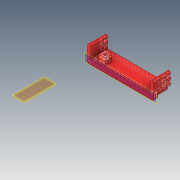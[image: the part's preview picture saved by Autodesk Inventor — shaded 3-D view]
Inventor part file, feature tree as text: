
AUTODESK INVENTOR PART (.ipt)
format: ipt  version: 2019 (Build 230136000, 136)  size: 296,960 bytes
history: native  units: mm
features: sketch x14, extrude x12, plane x4, projected_geometry x3, fillet x2
ambient origin geometry x8: Origin, YZ Plane, XZ Plane, XY Plane, X Axis, Y Axis, Z Axis, Center Point
bodies: Solid1 (feature_tree)
feature tree (35):
  extrude  "Extrusion1"  Depth=100.0mm
  extrude  "Extrusion2"  Depth=5.0mm
  extrude  "Extrusion3"  Depth=18.0mm TaperAngle=0.0deg
  extrude  "Extrusion4"  Depth=3.0mm
  fillet  "Fillet1"  Radius=20.0mm
  sketch  "Sketch11"  dims[d14=3.0mm d15=7.0mm]
  sketch  "Sketch12"  dims[d16=1.5mm d17=1.5mm]
  extrude  "Extrusion8"  Depth=7.0mm
  extrude  "Extrusion9"  Depth=1.5mm
  fillet  "Fillet4"  Radius=7.0mm
  extrude  "Extrusion10"  Depth=2.0mm
  extrude  "Extrusion11"  Depth=2.5mm TaperAngle=0.0deg
  sketch  "Sketch19"  dims[d41=8.0mm d42=20.0mm]
  plane  "Work Plane2"
  extrude  "Extrusion12"  TaperAngle=0.0deg  [1 undecoded]
  plane  "Work Plane3"
  extrude  "Extrusion13"  Depth=20.0mm
  extrude  "Extrusion14"  TaperAngle=0.0deg  [1 undecoded]
  plane  "Work Plane4"
  extrude  "Extrusion15"  Depth=13.0mm
  sketch  "Sketch1"  dims[d0=100.0mm d1=150.0mm]
  sketch  "Sketch3"  dims[d2=8.0mm d3=0.0mm d4=5.0mm]
  projected_geometry  "Projected Loop2"
  sketch  "Sketch4"  dims[d5=5.0mm d6=18.0mm d7=0.0mm]
  projected_geometry  "Projected Loop3"
  sketch  "Sketch6"  dims[d8=3.0mm d9=3.0mm d10=20.0mm d11=0.0mm]
  sketch  "Sketch15"  dims[d18=3.0mm d19=1.5mm d20=1.5mm d21=5.1mm d22=7.0mm]
  projected_geometry  "Projected Loop7"
  sketch  "Sketch16"  dims[d23=20.0mm d24=0.0mm d25=2.0mm]
  sketch  "Sketch17"  dims[d36=1.7mm d37=2.5mm d38=0.0mm]
  sketch  "Sketch18"  dims[d39=35.0mm d40=0.0mm]
  plane  "Work Plane1"
  sketch  "Sketch20"  dims[d43=0.0mm d44=0.0mm]
  sketch  "Sketch21"  dims[d45=25.0mm d46=13.0mm]
  sketch  "Sketch22"  dims[d47=16.0mm d48=0.0mm d49=1.0mm d50=4.2mm d51=3.5mm d52=9.0mm d53=4.2mm d54=6.0mm d55=12.0mm d56=8.0mm d57=0.0mm d60=4.3mm d61=4.3mm d62=30.8mm d64=5.0mm d65=0.0mm d66=0.0mm d67=100.0mm d69=-4.0mm d70=-2.0mm d71=10.0mm d72=0.0mm d73=-26.0mm d74=10.0mm d75=0.0mm d76=4.2mm d77=2.0mm d78=10.0mm d79=5.0mm d80=10.0mm d81=10.0mm d82=5.0mm d83=10.0mm d84=0.0mm d85=-1.5mm d86=3.15mm d87=0.0mm d88=7.0mm]
note: 2 required parameter values undecoded (feature->parameter linkage not recoverable at this tier; creation-order binding heuristic only, values carry confidence <= 0.55)
